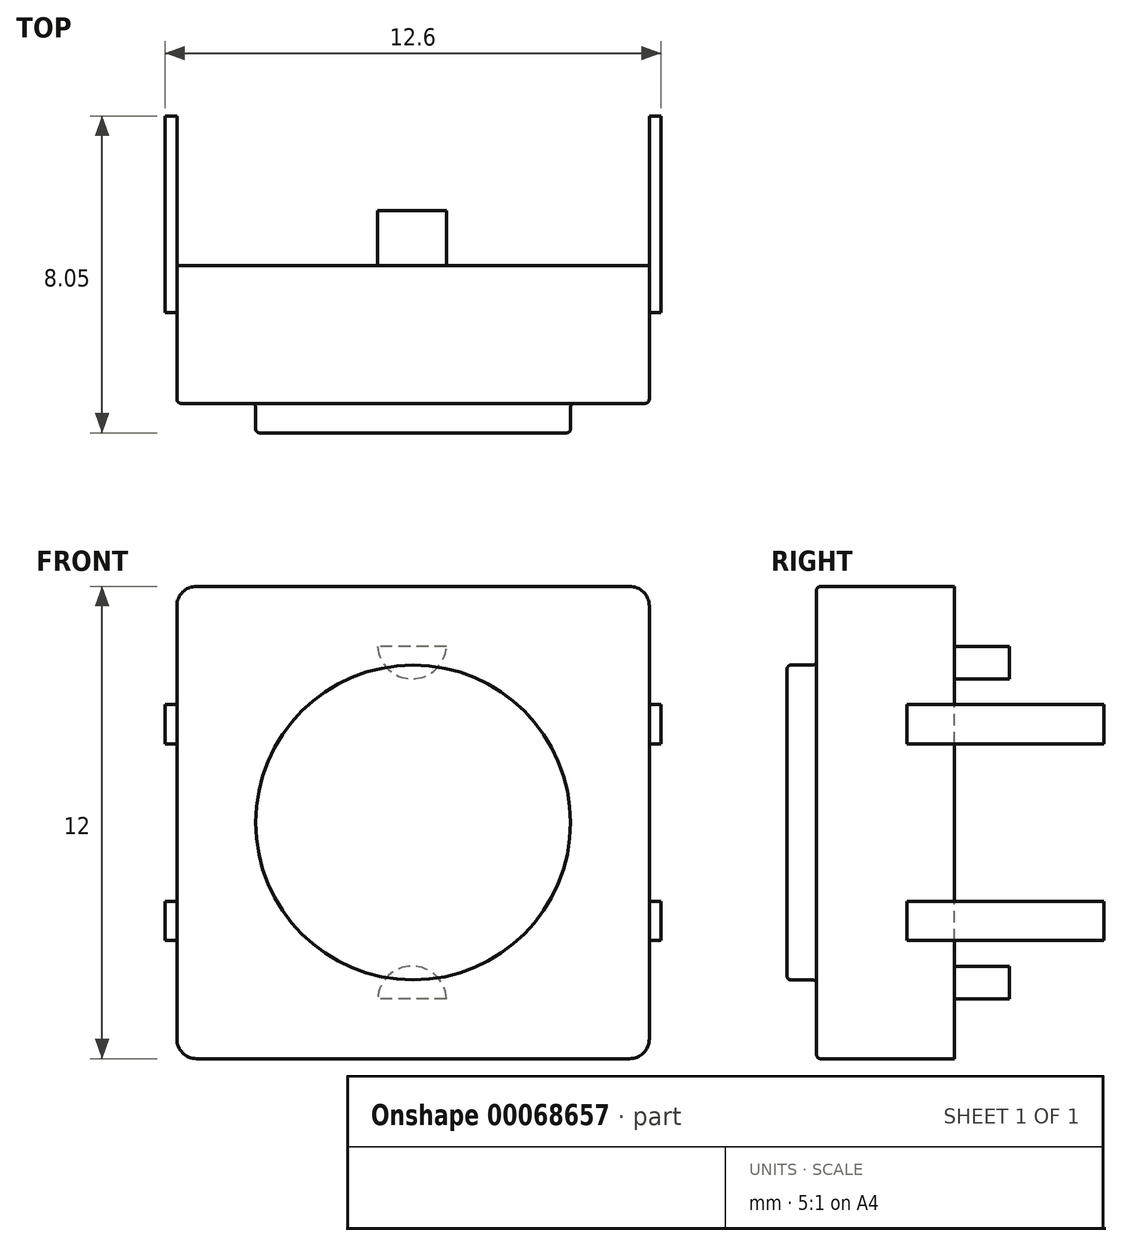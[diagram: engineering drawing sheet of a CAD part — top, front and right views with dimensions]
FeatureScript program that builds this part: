
annotation { "Feature Type Name" : "Feature", "Feature Type Description" : "" }
export const myFeature = defineFeature(function(context is Context, id is Id, definition is map)
    precondition{}
    {
        {
            var Q0;
            Q0=qCreatedBy(makeId("Front.planeOp"),FACE);
            var sketch = newSketch(context, id + "F0", { "sketchPlane" : qUnion([Q0])});
            skLineSegment(sketch, "E0.rect.bottom", {"start": v(6, -6) * mm, "end": v(-6, -6) * mm});
            skLineSegment(sketch, "E0.rect.top", {"start": v(6, 6) * mm, "end": v(-6, 6) * mm});
            skLineSegment(sketch, "E0.rect.left", {"start": v(6, -6) * mm, "end": v(6, 6) * mm});
            skLineSegment(sketch, "E0.rect.right", {"start": v(-6, -6) * mm, "end": v(-6, 6) * mm});
            skPoint(sketch, "E0.rect.middle", {"position": v(0, 0) * mm});
            skSolve(sketch);
        }
        {
            var Q0;
            Q0=makeQuery(id+"F0.imprint","IMPRINT",FACE,{"disambiguationData":[TD([[makeQuery(id+"F0.imprint","IMPRINT",EDGE,{"derivedFrom":sQuery(id+"F0.wireOp",EDGE,"E0.rect.bottom")}),-1.0]])]});
            extrude(context, id + "F1", {"entities" : qUnion([Q0]), "depth" : 3.5 * mm});
        }
        {
            var Q0;
            Q0=makeQuery(id+"F1.opExtrude","SWEPT_EDGE",EDGE,{"disambiguationData":[OSD([sQuery(id+"F0.wireOp",EDGE,"E0.rect.top"),sQuery(id+"F0.wireOp",EDGE,"E0.rect.left")])]});
            var Q1;
            Q1=makeQuery(id+"F1.opExtrude","SWEPT_EDGE",EDGE,{"disambiguationData":[OSD([sQuery(id+"F0.wireOp",EDGE,"E0.rect.bottom"),sQuery(id+"F0.wireOp",EDGE,"E0.rect.left")])]});
            var Q2;
            Q2=makeQuery(id+"F1.opExtrude","SWEPT_EDGE",EDGE,{"disambiguationData":[OSD([sQuery(id+"F0.wireOp",EDGE,"E0.rect.bottom"),sQuery(id+"F0.wireOp",EDGE,"E0.rect.right")])]});
            var Q3;
            Q3=makeQuery(id+"F1.opExtrude","SWEPT_EDGE",EDGE,{"disambiguationData":[OSD([sQuery(id+"F0.wireOp",EDGE,"E0.rect.top"),sQuery(id+"F0.wireOp",EDGE,"E0.rect.right")])]});
            fillet(context, id + "F2", {"entities" : qUnion([Q0, Q1, Q2, Q3]), "radius" : .5 * mm, "tangentPropagation" : true, "allowEdgeOverflow" : false});
        }
        {
            var Q0;
            Q0=makeQuery(id+"F1.opExtrude","CAP_FACE",FACE,{"disambiguationData":[OSD([sQuery(id+"F0.wireOp",EDGE,"E0.rect.bottom"),sQuery(id+"F0.wireOp",EDGE,"E0.rect.top"),sQuery(id+"F0.wireOp",EDGE,"E0.rect.left"),sQuery(id+"F0.wireOp",EDGE,"E0.rect.right")])],"isStart":false});
            var sketch = newSketch(context, id + "F3", { "sketchPlane" : qUnion([Q0])});
            skCircle(sketch, "E1", {"center": v(0, 0) * mm, "radius": 4 * mm});
            skSolve(sketch);
        }
        {
            var Q0;
            Q0=makeQuery(id+"F3.imprint","IMPRINT",FACE,{"disambiguationData":[TD([[makeQuery(id+"F3.imprint","IMPRINT",EDGE,{"derivedFrom":sQuery(id+"F3.wireOp",EDGE,"E1")}),1.0]])]});
            extrude(context, id + "F4", {"entities" : qUnion([Q0]), "operationType" : NewBodyOperationType.ADD, "depth" : .75 * mm});
        }
        {
            var Q0;
            Q0=makeQuery(id+"F4.opExtrude","CAP_EDGE",EDGE,{"disambiguationData":[OSD([sQuery(id+"F3.wireOp",EDGE,"E1")])],"isStart":false});
            fillet(context, id + "F5", {"entities" : qUnion([Q0]), "radius" : .1 * mm, "tangentPropagation" : true, "allowEdgeOverflow" : false});
        }
        {
            var Q0;
            Q0=makeQuery(id+"F1.opExtrude","CAP_FACE",FACE,{"disambiguationData":[OSD([sQuery(id+"F0.wireOp",EDGE,"E0.rect.bottom"),sQuery(id+"F0.wireOp",EDGE,"E0.rect.top"),sQuery(id+"F0.wireOp",EDGE,"E0.rect.left"),sQuery(id+"F0.wireOp",EDGE,"E0.rect.right")])],"isStart":false});
            fillet(context, id + "F6", {"entities" : qUnion([Q0]), "radius" : .1 * mm, "tangentPropagation" : true, "allowEdgeOverflow" : false});
        }
        {
            var Q0;
            Q0=makeQuery(id+"F1.opExtrude","SWEPT_FACE",FACE,{"disambiguationData":[OSD([sQuery(id+"F0.wireOp",EDGE,"E0.rect.right")])]});
            var sketch = newSketch(context, id + "F7", { "sketchPlane" : qUnion([Q0])});
            skPoint(sketch, "E2", {"position": v(0, -2) * mm});
            skLineSegment(sketch, "E3", {"start": v(0, -2) * mm, "end": v(3.4, -2) * mm, "construction": true});
            skPoint(sketch, "E4", {"position": v(1.2, -2) * mm});
            skLineSegment(sketch, "E5.bottom", {"start": v(1.2, -2) * mm, "end": v(-3.8, -2) * mm});
            skLineSegment(sketch, "E5.top", {"start": v(1.2, -3) * mm, "end": v(-3.8, -3) * mm});
            skLineSegment(sketch, "E5.left", {"start": v(1.2, -2) * mm, "end": v(1.2, -3) * mm});
            skLineSegment(sketch, "E5.right", {"start": v(-3.8, -2) * mm, "end": v(-3.8, -3) * mm});
            skLineSegment(sketch, "E6", {"start": v(1.2, -2) * mm, "end": v(1.2, 3.38) * mm, "construction": true});
            skPoint(sketch, "E7", {"position": v(1.2, 2) * mm});
            skLineSegment(sketch, "E8.bottom", {"start": v(1.2, 2) * mm, "end": v(-3.8, 2) * mm});
            skLineSegment(sketch, "E8.top", {"start": v(1.2, 3) * mm, "end": v(-3.8, 3) * mm});
            skLineSegment(sketch, "E8.left", {"start": v(1.2, 2) * mm, "end": v(1.2, 3) * mm});
            skLineSegment(sketch, "E8.right", {"start": v(-3.8, 2) * mm, "end": v(-3.8, 3) * mm});
            skSolve(sketch);
        }
        {
            var Q0;
            {var subQ0=sQuery(id+"F7.wireOp",EDGE,"E8.right");Q0=makeQuery(id+"F7.imprint","IMPRINT",FACE,{"disambiguationData":[TD([[makeQuery(id+"F7.imprint","IMPRINT",EDGE,{"derivedFrom":subQ0}),-1.0]])]});}
            var Q1;
            {var subQ0=sQuery(id+"F7.wireOp",EDGE,"E8.left");Q1=makeQuery(id+"F7.imprint","IMPRINT",FACE,{"disambiguationData":[TD([[makeQuery(id+"F7.imprint","IMPRINT",EDGE,{"derivedFrom":subQ0}),1.0]])]});}
            var Q2;
            {var subQ0=sQuery(id+"F7.wireOp",EDGE,"E5.left");Q2=makeQuery(id+"F7.imprint","IMPRINT",FACE,{"disambiguationData":[TD([[makeQuery(id+"F7.imprint","IMPRINT",EDGE,{"derivedFrom":subQ0}),-1.0]])]});}
            var Q3;
            {var subQ0=sQuery(id+"F7.wireOp",EDGE,"E5.right");Q3=makeQuery(id+"F7.imprint","IMPRINT",FACE,{"disambiguationData":[TD([[makeQuery(id+"F7.imprint","IMPRINT",EDGE,{"derivedFrom":subQ0}),1.0]])]});}
            extrude(context, id + "F8", {"entities" : qUnion([Q0, Q1, Q2, Q3]), "operationType" : NewBodyOperationType.ADD, "depth" : .3 * mm});
        }
        {
            var Q0;
            Q0=makeQuery(id+"F1.opExtrude","SWEPT_FACE",FACE,{"disambiguationData":[OSD([sQuery(id+"F0.wireOp",EDGE,"E0.rect.left")])]});
            var sketch = newSketch(context, id + "F9", { "sketchPlane" : qUnion([Q0])});
            skPoint(sketch, "E9", {"position": v(-1.2, -2) * mm});
            skPoint(sketch, "E10", {"position": v(-1.2, 2) * mm});
            skLineSegment(sketch, "E11.bottom", {"start": v(-1.2, 2) * mm, "end": v(3.8, 2) * mm});
            skLineSegment(sketch, "E11.top", {"start": v(-1.2, 3) * mm, "end": v(3.8, 3) * mm});
            skLineSegment(sketch, "E11.left", {"start": v(-1.2, 2) * mm, "end": v(-1.2, 3) * mm});
            skLineSegment(sketch, "E11.right", {"start": v(3.8, 2) * mm, "end": v(3.8, 3) * mm});
            skLineSegment(sketch, "E12.bottom", {"start": v(-1.2, -2) * mm, "end": v(3.8, -2) * mm});
            skLineSegment(sketch, "E12.top", {"start": v(-1.2, -3) * mm, "end": v(3.8, -3) * mm});
            skLineSegment(sketch, "E12.left", {"start": v(-1.2, -2) * mm, "end": v(-1.2, -3) * mm});
            skLineSegment(sketch, "E12.right", {"start": v(3.8, -2) * mm, "end": v(3.8, -3) * mm});
            skSolve(sketch);
        }
        {
            var Q0;
            {var subQ0=sQuery(id+"F9.wireOp",EDGE,"E11.left");Q0=makeQuery(id+"F9.imprint","IMPRINT",FACE,{"disambiguationData":[TD([[makeQuery(id+"F9.imprint","IMPRINT",EDGE,{"derivedFrom":subQ0}),-1.0]])]});}
            var Q1;
            {var subQ0=sQuery(id+"F9.wireOp",EDGE,"E11.right");Q1=makeQuery(id+"F9.imprint","IMPRINT",FACE,{"disambiguationData":[TD([[makeQuery(id+"F9.imprint","IMPRINT",EDGE,{"derivedFrom":subQ0}),1.0]])]});}
            var Q2;
            {var subQ0=sQuery(id+"F9.wireOp",EDGE,"E12.left");Q2=makeQuery(id+"F9.imprint","IMPRINT",FACE,{"disambiguationData":[TD([[makeQuery(id+"F9.imprint","IMPRINT",EDGE,{"derivedFrom":subQ0}),1.0]])]});}
            var Q3;
            {var subQ0=sQuery(id+"F9.wireOp",EDGE,"E12.right");Q3=makeQuery(id+"F9.imprint","IMPRINT",FACE,{"disambiguationData":[TD([[makeQuery(id+"F9.imprint","IMPRINT",EDGE,{"derivedFrom":subQ0}),-1.0]])]});}
            extrude(context, id + "F10", {"entities" : qUnion([Q0, Q1, Q2, Q3]), "operationType" : NewBodyOperationType.ADD, "depth" : .3 * mm});
        }
        {
            var Q0;
            Q0=makeQuery(id+"F1.opExtrude","CAP_FACE",FACE,{"disambiguationData":[OSD([sQuery(id+"F0.wireOp",EDGE,"E0.rect.bottom"),sQuery(id+"F0.wireOp",EDGE,"E0.rect.top"),sQuery(id+"F0.wireOp",EDGE,"E0.rect.left"),sQuery(id+"F0.wireOp",EDGE,"E0.rect.right")])],"isStart":true});
            var sketch = newSketch(context, id + "F11", { "sketchPlane" : qUnion([Q0])});
            skPoint(sketch, "E13", {"position": v(-0.85, 4.47) * mm});
            skPoint(sketch, "E14", {"position": v(0.9, 4.47) * mm});
            skPoint(sketch, "E15", {"position": v(0, 3.65) * mm});
            skLineSegment(sketch, "E16", {"start": v(-0.85, 4.47) * mm, "end": v(0.9, 4.47) * mm});
            skArc(sketch, "E17", {"start": v(-0.85, 4.47) * mm, "mid": v(0.02, 3.65) * mm, "end": v(0.9, 4.47) * mm});
            skPoint(sketch, "E18", {"position": v(0, -3.65) * mm});
            skPoint(sketch, "E19", {"position": v(-0.85, -4.47) * mm});
            skPoint(sketch, "E20", {"position": v(0.9, -4.47) * mm});
            skArc(sketch, "E21", {"start": v(0.9, -4.47) * mm, "mid": v(0.02, -3.65) * mm, "end": v(-0.85, -4.47) * mm});
            skLineSegment(sketch, "E22", {"start": v(-0.85, -4.47) * mm, "end": v(0.9, -4.47) * mm});
            skSolve(sketch);
        }
        {
            var Q0;
            Q0=makeQuery(id+"F11.imprint","IMPRINT",FACE,{"disambiguationData":[TD([[makeQuery(id+"F11.imprint","IMPRINT",EDGE,{"derivedFrom":sQuery(id+"F11.wireOp",EDGE,"E16")}),-1.0]])]});
            var Q1;
            Q1=makeQuery(id+"F11.imprint","IMPRINT",FACE,{"disambiguationData":[TD([[makeQuery(id+"F11.imprint","IMPRINT",EDGE,{"derivedFrom":sQuery(id+"F11.wireOp",EDGE,"E21")}),1.0]])]});
            extrude(context, id + "F12", {"entities" : qUnion([Q0, Q1]), "operationType" : NewBodyOperationType.ADD, "depth" : 1.4 * mm});
        }
    });
